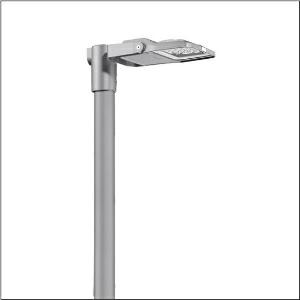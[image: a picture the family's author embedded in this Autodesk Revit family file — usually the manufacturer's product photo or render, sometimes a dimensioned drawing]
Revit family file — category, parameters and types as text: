
# Revit family: floodlight_fl_21_iq_micro___pl52_5xa7762a2d3a_f78f
name_source: partatom
category: Lighting Fixtures
units: mm (PartAtom-declared; Revit-internal decimal feet)

## family parameters
Cut with Voids When Loaded = No
Host = Face
Light Source = No
Part Type = Normal
Room Calculation Point = No
Round Connector Dimension = Use Diameter
Shared = No

## types (1)
- --- (1 x LED, 2890 lm, 23.1 W, 3000K)
    Apparent Load = 23 VA
    CIE Flux Codes = 26 60 98 100 100
    Color Rendering = 70
    Color Temperature = 3000K
    Default Elevation = 1800 mm
    Description = Floodlight FL 21 iQ micro, floodlight, primary light control with lens, of PMMA, primary optical cover: protective disc, of toughened safety glass, transparent, light distribution: PL52, light emission: direct distribution, installation type: surface-mounted, LED, High Power LED, rated luminous flux: 2.890lm, luminous efficacy: 125lm/W, light colour: 730, colour temperature: 3000K, control: Auto-Match, Temp-Guard, Night-Set, Smart-Wire, Desk-Remote (wireless, voltage-free reading and setting of iQ features in the workshop via application-optimized NFC function/RFID function), optimised constant luminous flux control (CLO 2.0), Street-Remote, with terminal, 6-pole, mains connection: 220..240V, AC, 50/60Hz, start of lifetime: 23W, end of service life: 24W, reduction: 11W, luminaire housing, of diecast aluminium, powder-coated, Siteco® metallic grey (DB 702S), corrosivity category C5 mid according to DIN EN ISO 12944, sealing non-destructively replaceable, please order mast flange separately, mast bracket, of steel, galvanised, powder-coated, Siteco® metallic grey (DB 702S), protection rating (complete): IP66, insulation class (complete): insulation class II (safety insulation), certification: CE, ENEC, VDE, protection symbol: D, impact resistance: IK07, permissible operating ambient temperature: -40..+40°C, permissible operating ambient temperature for outdoor applications: -40..+50°C, standard: DIN EN 12944, LABS conformity tested according to VDMA 24364:2018-05, packaging unit: 1 piece

Light Distribution: PL52
    Height = 65 mm
    Lamp = 1 x LED
    Lamp Light Flux = 2890 lm
    Lamp Power = 23.1 W
    Lamp count = 1
    Length = 312 mm
    Luminous efficacy = 125 lm/W
    Manufacturer = Siteco
    ModVariant = No
    Model = 5XA7762A2D3A
    Number of Poles = 1
    OnlyDefault = Yes
    Power Factor = 1
    Product Name = Floodlight FL 21 iQ micro | PL52
    Product group = floodlight | pylon annexe
    ProductGroupID = 6200
    Protection Class = Protection class II
    Protection Degree = IP 66
    RLX_Detail_Level = 1
    RLX_Emergency_Light_Flux = 0 lm
    RLX_Emergency_Type = 0
    RLX_Emergency_Type_DB = No
    RlxData = <blob elided: 101953 chars, md5=4efdb5d7>
    Socket = socket
    Standby Power = 0 W
    System Light Flux = 2890 lm
    System Power = 23 W
    Type Comments = factory setting: luminous flux: 100 % | dim-lin: 254 | 455 mA
    Type Image = l_1007121.jpg
    URL = http://relux.com
    VarID = @adj_129031
    Voltage = 0 V
    Weight = 0.00 kg
    Width = 230 mm

## geometry (parser evidence)
native form markers: Blend x4, Sweep x11
no freeform markers — native parametric forms only
